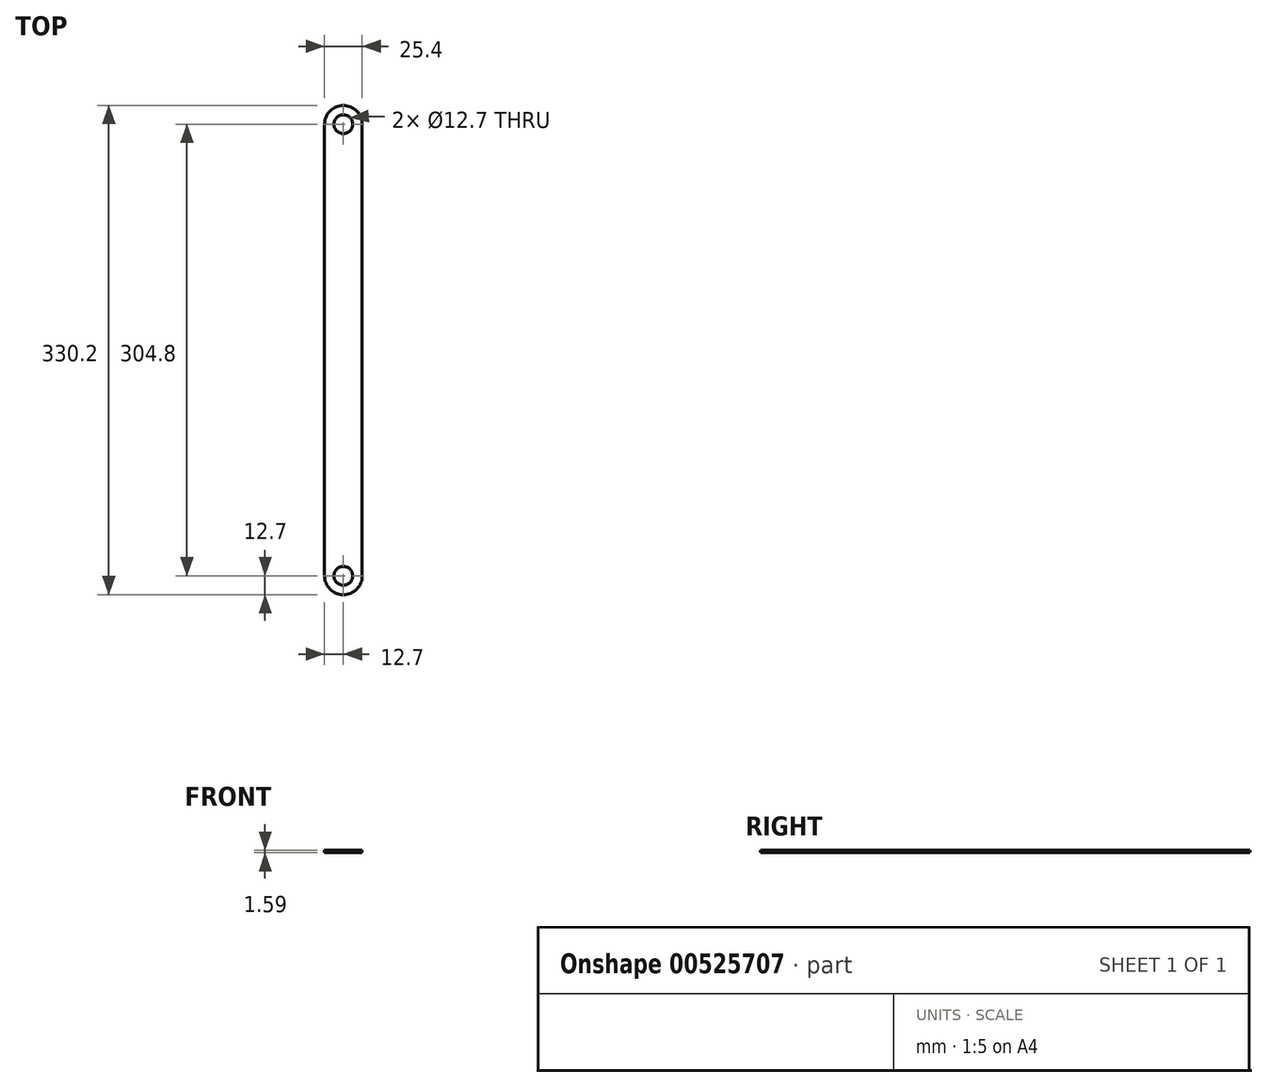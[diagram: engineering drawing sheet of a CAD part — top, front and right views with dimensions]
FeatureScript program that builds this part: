
annotation { "Feature Type Name" : "Feature", "Feature Type Description" : "" }
export const myFeature = defineFeature(function(context is Context, id is Id, definition is map)
    precondition{}
    {
        {
            var Q0;
            Q0=qCreatedBy(makeId("Top.planeOp"),FACE);
            var sketch = newSketch(context, id + "F0", { "sketchPlane" : qUnion([Q0])});
            skLineSegment(sketch, "E0.bottom", {"start": v(-12.7, 152.4) * mm, "end": v(12.7, 152.4) * mm});
            skLineSegment(sketch, "E0.top", {"start": v(-12.7, -152.4) * mm, "end": v(12.7, -152.4) * mm});
            skLineSegment(sketch, "E0.left", {"start": v(-12.7, 152.4) * mm, "end": v(-12.7, -152.4) * mm});
            skLineSegment(sketch, "E0.right", {"start": v(12.7, 152.4) * mm, "end": v(12.7, -152.4) * mm});
            skPoint(sketch, "E0.middle", {"position": v(0, 0) * mm});
            skArc(sketch, "E1", {"start": v(12.7, 152.4) * mm, "mid": v(0, 165.1) * mm, "end": v(-12.7, 152.4) * mm});
            skArc(sketch, "E2", {"start": v(-12.7, -152.4) * mm, "mid": v(0, -165.1) * mm, "end": v(12.7, -152.4) * mm});
            skLineSegment(sketch, "E3", {"start": v(0, 165.1) * mm, "end": v(0, -165.1) * mm});
            skCircle(sketch, "E4", {"center": v(0, 152.4) * mm, "radius": 6.35 * mm});
            skCircle(sketch, "E5", {"center": v(0, -152.4) * mm, "radius": 6.35 * mm});
            skSolve(sketch);
        }
        {
            var Q0;
            {var subQ5=sQuery(id+"F0.wireOp",EDGE,"E0.left");Q0=makeQuery(id+"F0.imprint","IMPRINT",FACE,{"disambiguationData":[TD([[makeQuery(id+"F0.imprint","IMPRINT",EDGE,{"derivedFrom":subQ5}),1.0]])]});}
            var Q1;
            {var subQ0=sQuery(id+"F0.wireOp",EDGE,"E0.right");Q1=makeQuery(id+"F0.imprint","IMPRINT",FACE,{"disambiguationData":[TD([[makeQuery(id+"F0.imprint","IMPRINT",EDGE,{"derivedFrom":subQ0}),-1.0]])]});}
            var Q2;
            {var subQ0=sQuery(id+"F0.wireOp",EDGE,"E1");var subQ5=sQuery(id+"F0.wireOp",EDGE,"E3");var subQ6=makeQuery(id+"F0.imprint","INTERSECT",VERTEX,{"derivedFrom":[subQ0,subQ5]});Q2=makeQuery(id+"F0.imprint","IMPRINT",FACE,{"disambiguationData":[TD([[makeQuery(id+"F0.imprint","IMPRINT",EDGE,{"disambiguationData":[TD([[subQ6,-1.0]])],"derivedFrom":subQ5}),-1.0]])]});}
            var Q3;
            {var subQ0=sQuery(id+"F0.wireOp",EDGE,"E1");var subQ5=sQuery(id+"F0.wireOp",EDGE,"E3");var subQ6=makeQuery(id+"F0.imprint","INTERSECT",VERTEX,{"derivedFrom":[subQ0,subQ5]});Q3=makeQuery(id+"F0.imprint","IMPRINT",FACE,{"disambiguationData":[TD([[makeQuery(id+"F0.imprint","IMPRINT",EDGE,{"disambiguationData":[TD([[subQ6,-1.0]])],"derivedFrom":subQ5}),1.0]])]});}
            var Q4;
            {var subQ0=sQuery(id+"F0.wireOp",EDGE,"E2");var subQ5=sQuery(id+"F0.wireOp",EDGE,"E3");var subQ6=makeQuery(id+"F0.imprint","INTERSECT",VERTEX,{"derivedFrom":[subQ0,subQ5]});Q4=makeQuery(id+"F0.imprint","IMPRINT",FACE,{"disambiguationData":[TD([[makeQuery(id+"F0.imprint","IMPRINT",EDGE,{"disambiguationData":[TD([[subQ6,1.0]])],"derivedFrom":subQ5}),1.0]])]});}
            var Q5;
            {var subQ0=sQuery(id+"F0.wireOp",EDGE,"E2");var subQ5=sQuery(id+"F0.wireOp",EDGE,"E3");var subQ6=makeQuery(id+"F0.imprint","INTERSECT",VERTEX,{"derivedFrom":[subQ0,subQ5]});Q5=makeQuery(id+"F0.imprint","IMPRINT",FACE,{"disambiguationData":[TD([[makeQuery(id+"F0.imprint","IMPRINT",EDGE,{"disambiguationData":[TD([[subQ6,1.0]])],"derivedFrom":subQ5}),-1.0]])]});}
            extrude(context, id + "F1", {"entities" : qUnion([Q0, Q1, Q2, Q3, Q4, Q5]), "depth" : 1.59 * mm, "offsetDistance" : 25.4 * mm});
        }
    });
